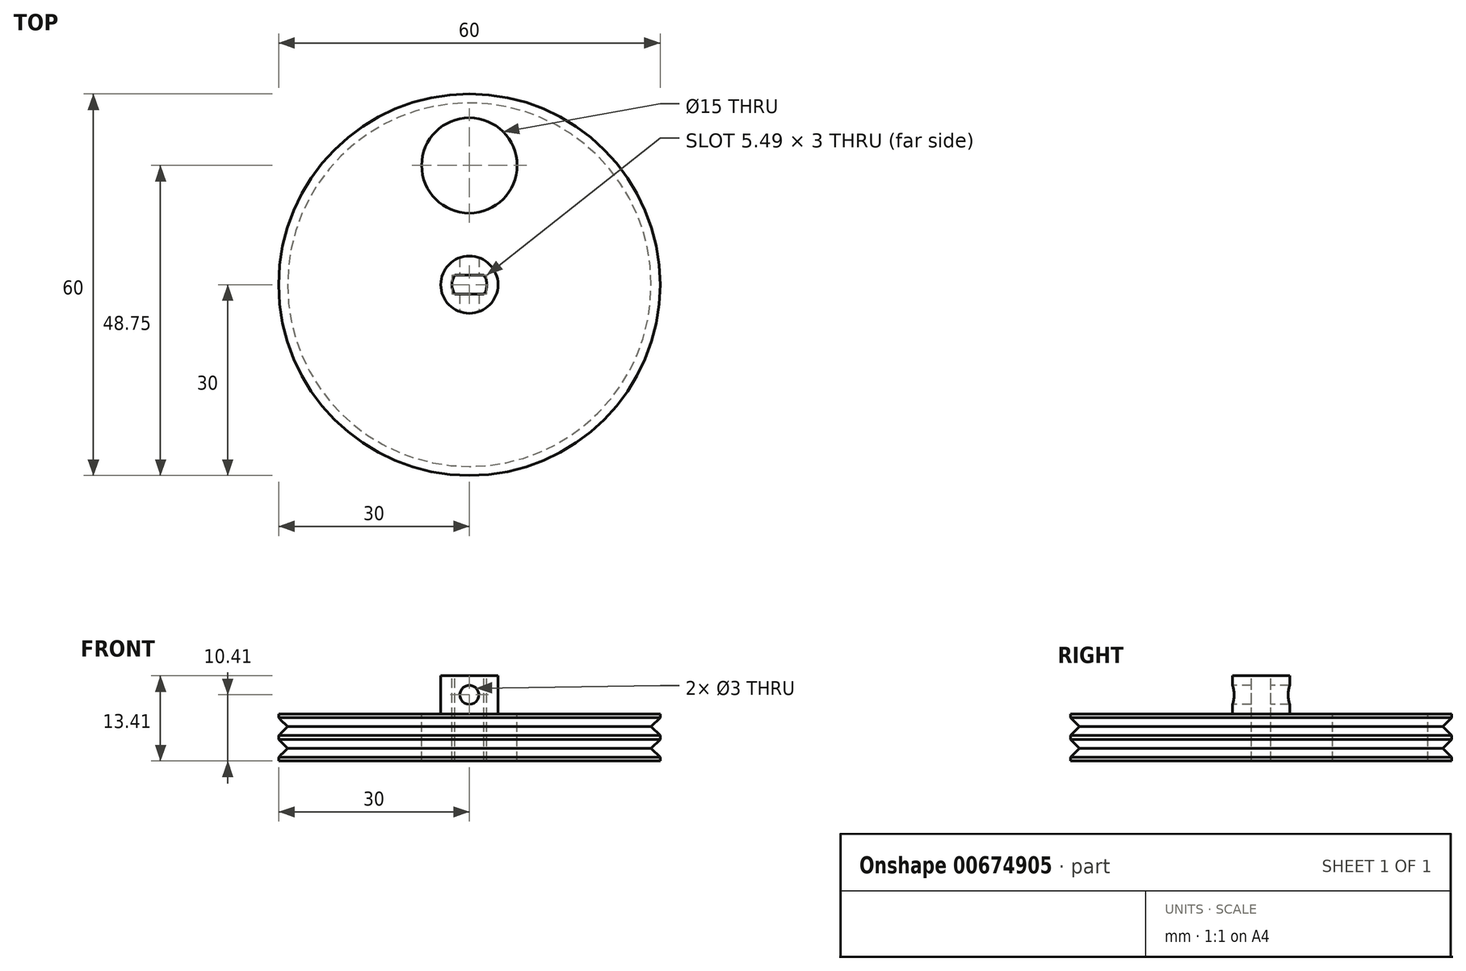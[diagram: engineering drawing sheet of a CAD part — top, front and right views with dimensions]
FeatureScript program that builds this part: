
annotation { "Feature Type Name" : "Feature", "Feature Type Description" : "" }
export const myFeature = defineFeature(function(context is Context, id is Id, definition is map)
    precondition{}
    {
        {
            var Q0;
            Q0=qCreatedBy(makeId("Top.planeOp"),FACE);
            var sketch = newSketch(context, id + "F0", { "sketchPlane" : qUnion([Q0])});
            skCircle(sketch, "E0", {"center": v(0, 0) * mm, "radius": 30 * mm});
            skCircle(sketch, "E1", {"center": v(0, 0) * mm, "radius": 4.5 * mm});
            skSolve(sketch);
        }
        {
            var Q0;
            Q0=makeQuery(id+"F0.imprint","IMPRINT",FACE,{"disambiguationData":[TD([[makeQuery(id+"F0.imprint","IMPRINT",EDGE,{"derivedFrom":sQuery(id+"F0.wireOp",EDGE,"E1")}),1.0]])]});
            var Q1;
            Q1=makeQuery(id+"F0.imprint","IMPRINT",FACE,{"disambiguationData":[TD([[makeQuery(id+"F0.imprint","IMPRINT",EDGE,{"derivedFrom":sQuery(id+"F0.wireOp",EDGE,"E0")}),1.0]])]});
            extrude(context, id + "F1", {"entities" : qUnion([Q0, Q1]), "oppositeDirection" : true, "depth" : 7.4 * mm, "offsetDistance" : 25 * mm});
        }
        {
            var Q0;
            Q0=makeQuery(id+"F0.imprint","IMPRINT",FACE,{"disambiguationData":[TD([[makeQuery(id+"F0.imprint","IMPRINT",EDGE,{"derivedFrom":sQuery(id+"F0.wireOp",EDGE,"E1")}),1.0]])]});
            extrude(context, id + "F2", {"entities" : qUnion([Q0]), "operationType" : NewBodyOperationType.ADD, "depth" : 6 * mm, "offsetDistance" : 25 * mm});
        }
        {
            var Q0;
            Q0=qCreatedBy(makeId("Front.planeOp"),FACE);
            var sketch = newSketch(context, id + "F3", { "sketchPlane" : qUnion([Q0])});
            skCircle(sketch, "E2", {"center": v(0, 3) * mm, "radius": 1.5 * mm});
            skSolve(sketch);
        }
        {
            var Q0;
            Q0=qSketchRegion(id+"F3",true);
            extrude(context, id + "F4", {"entities" : qUnion([Q0]), "operationType" : NewBodyOperationType.REMOVE, "endBound" : BoundingType.SYMMETRIC, "oppositeDirection" : true, "depth" : 25 * mm, "offsetDistance" : 25 * mm});
        }
        {
            var Q0;
            Q0=makeQuery(id+"F2.opExtrude","CAP_FACE",FACE,{"disambiguationData":[OSD([sQuery(id+"F0.wireOp",EDGE,"E1")])],"isStart":false});
            var sketch = newSketch(context, id + "F5", { "sketchPlane" : qUnion([Q0])});
            skLineSegment(sketch, "E3.bottom", {"start": v(-2.3, -1.5) * mm, "end": v(2.3, -1.5) * mm});
            skLineSegment(sketch, "E3.top", {"start": v(-2.3, 1.5) * mm, "end": v(2.3, 1.5) * mm});
            skLineSegment(sketch, "E3.left", {"start": v(-2.3, -1.5) * mm, "end": v(-2.3, 1.5) * mm});
            skLineSegment(sketch, "E3.right", {"start": v(2.3, -1.5) * mm, "end": v(2.3, 1.5) * mm});
            skPoint(sketch, "E3.middle", {"position": v(0, 0) * mm});
            skArc(sketch, "E4", {"start": v(-2.3, 1.5) * mm, "mid": v(-2.75, 0) * mm, "end": v(-2.3, -1.5) * mm});
            skArc(sketch, "E5", {"start": v(2.3, -1.5) * mm, "mid": v(2.75, 0) * mm, "end": v(2.3, 1.5) * mm});
            skSolve(sketch);
        }
        {
            var Q0;
            Q0=qSketchRegion(id+"F5",true);
            var Q1;
            Q1=makeQuery(id+"F1.opExtrude","CAP_FACE",FACE,{"disambiguationData":[OSD([sQuery(id+"F0.wireOp",EDGE,"E0")])],"isStart":false});
            extrude(context, id + "F6", {"entities" : qUnion([Q0]), "operationType" : NewBodyOperationType.REMOVE, "endBound" : BoundingType.UP_TO_SURFACE, "oppositeDirection" : true, "depth" : 9.4 * mm, "endBoundEntityFace" : qUnion([Q1]), "offsetDistance" : 25 * mm});
        }
        {
            var Q0;
            Q0=qCreatedBy(makeId("Front.planeOp"),FACE);
            var sketch = newSketch(context, id + "F7", { "sketchPlane" : qUnion([Q0])});
            skLineSegment(sketch, "E6", {"start": v(30, 0) * mm, "end": v(30, -4) * mm, "construction": true});
            skLineSegment(sketch, "E7", {"start": v(30, -0.59) * mm, "end": v(28.59, -2) * mm});
            skLineSegment(sketch, "E8", {"start": v(28.59, -2) * mm, "end": v(30, -3.41) * mm});
            skLineSegment(sketch, "E9", {"start": v(30, -2) * mm, "end": v(25.84, -2) * mm, "construction": true});
            skLineSegment(sketch, "E10", {"start": v(0, 13.1) * mm, "end": v(0, -11.57) * mm, "construction": true});
            skLineSegment(sketch, "E11", {"start": v(30, -0.59) * mm, "end": v(30, -3.41) * mm});
            skLineSegment(sketch, "E12", {"start": v(30, 0) * mm, "end": v(30, -8) * mm});
            skLineSegment(sketch, "E13", {"start": v(30, -4) * mm, "end": v(28.59, -5.41) * mm});
            skLineSegment(sketch, "E14", {"start": v(28.59, -5.41) * mm, "end": v(30, -6.83) * mm});
            skSolve(sketch);
        }
        {
            var Q0;
            Q0=qSketchRegion(id+"F7",true);
            var Q1;
            Q1=qConstructionFilter(qBodyType(qCreatedBy(id+"F7",EDGE),BodyType.WIRE),ConstructionObject.NO);
            var Q2;
            Q2=sQuery(id+"F7.wireOp",EDGE,"E10");
            revolve(context, id + "F8", {"operationType" : NewBodyOperationType.REMOVE, "entities" : qUnion([Q0]), "surfaceEntities" : qUnion([Q1]), "axis" : qUnion([Q2]), "revolveType" : RevolveType.FULL, "oppositeDirection" : true});
        }
        {
            var Q0;
            Q0=makeQuery(id+"F0.imprint","IMPRINT",FACE,{"disambiguationData":[TD([[makeQuery(id+"F0.imprint","IMPRINT",EDGE,{"derivedFrom":sQuery(id+"F0.wireOp",EDGE,"E0")}),1.0]])]});
            var sketch = newSketch(context, id + "F9", { "sketchPlane" : qUnion([Q0])});
            skCircle(sketch, "E15", {"center": v(0, 18.75) * mm, "radius": 7.5 * mm});
            skSolve(sketch);
        }
        {
            var Q0;
            Q0=qSketchRegion(id+"F9",true);
            extrude(context, id + "F10", {"entities" : qUnion([Q0]), "operationType" : NewBodyOperationType.REMOVE, "oppositeDirection" : true, "depth" : 25 * mm, "offsetDistance" : 25 * mm});
        }
    });
